# Revit family: Access_Door-Acudor-Universal_Flush-UF-5500_Series
name_source: partatom
category: Specialty Equipment
revit_build: Autodesk Revit 2014 (Build: 20130308_1515(x64)
units: mm (PartAtom-declared; Revit-internal decimal feet)

## types (6) — shared parameters
Allen Head Cam Latch = No
Assembly Code = C1020700
Cylinder Lock = No
Default Elevation = 48"
Description = Universal Flush Access Door
Finish = Galvanized Steel-Baked White Polyester Powder Coat
Installation Type = Wall Mounted
Latch Count = 2
Length = 1 5/16"
Manufacturer = Acudor
Material = Galvanized Steel-Baked White Polyester Powder Coat
Mortise Cylinder Lock (Prepare for/or Installed) = No
Product Documentation Link = https://acudor.com
Product Page URL = https://acudor.com
Rim Cylinder Lock = No
Spanner Head Cam Latch = No
Torx Cam Latch = No
URL = http://acudor.com

## per-type parameters (varying)
| type | Array Visibility | First Offset | Height | Latch Spacing | Single Latch Visibility | Width |
| UF-5500 6x6 | Yes | 1 1/2" | 6" | 3" | No | 6" |
| UF-5500 8x8 | No | 2" | 8" | 4" | Yes | 8" |
| UF-5500 12x12 | No | 3" | 12" | 6" | Yes | 12" |
| UF-5500 24x24 | Yes | 6" | 24" | 12" | No | 24" |
| UF-5500 18x18 | No | 4 1/2" | 18" | 9" | Yes | 18" |
| UF-5500 15x15 | No | 3 3/4" | 15" | 7 1/2" | Yes | 15" |

note: column(s) folded — value = type name in every type: Model

## geometry (parser evidence)
native form markers: Sweep x3
no freeform markers — native parametric forms only
